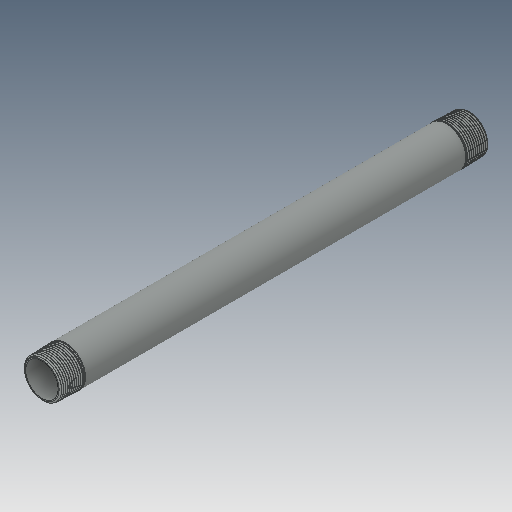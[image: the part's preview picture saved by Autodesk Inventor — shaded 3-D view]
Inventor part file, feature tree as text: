
AUTODESK INVENTOR PART (.ipt)
format: ipt  version: 2023.5 (Build 275446000, 446)  size: 1,338,368 bytes
history: native  units: in
note: dims shown in document units (in); Inventor stores cm internally (conversion verified against a paired STEP export)
features: revolve x1
ambient origin geometry x8: Origin, YZ Plane, XZ Plane, XY Plane, X Axis, Y Axis, Z Axis, Center Point
bodies: Solid1 (feature_tree)
feature tree (1):
  revolve  "Revolve2"  [1 undecoded]
note: 1 required parameter value undecoded (feature->parameter linkage not recoverable at this tier; creation-order binding heuristic only, values carry confidence <= 0.55)
